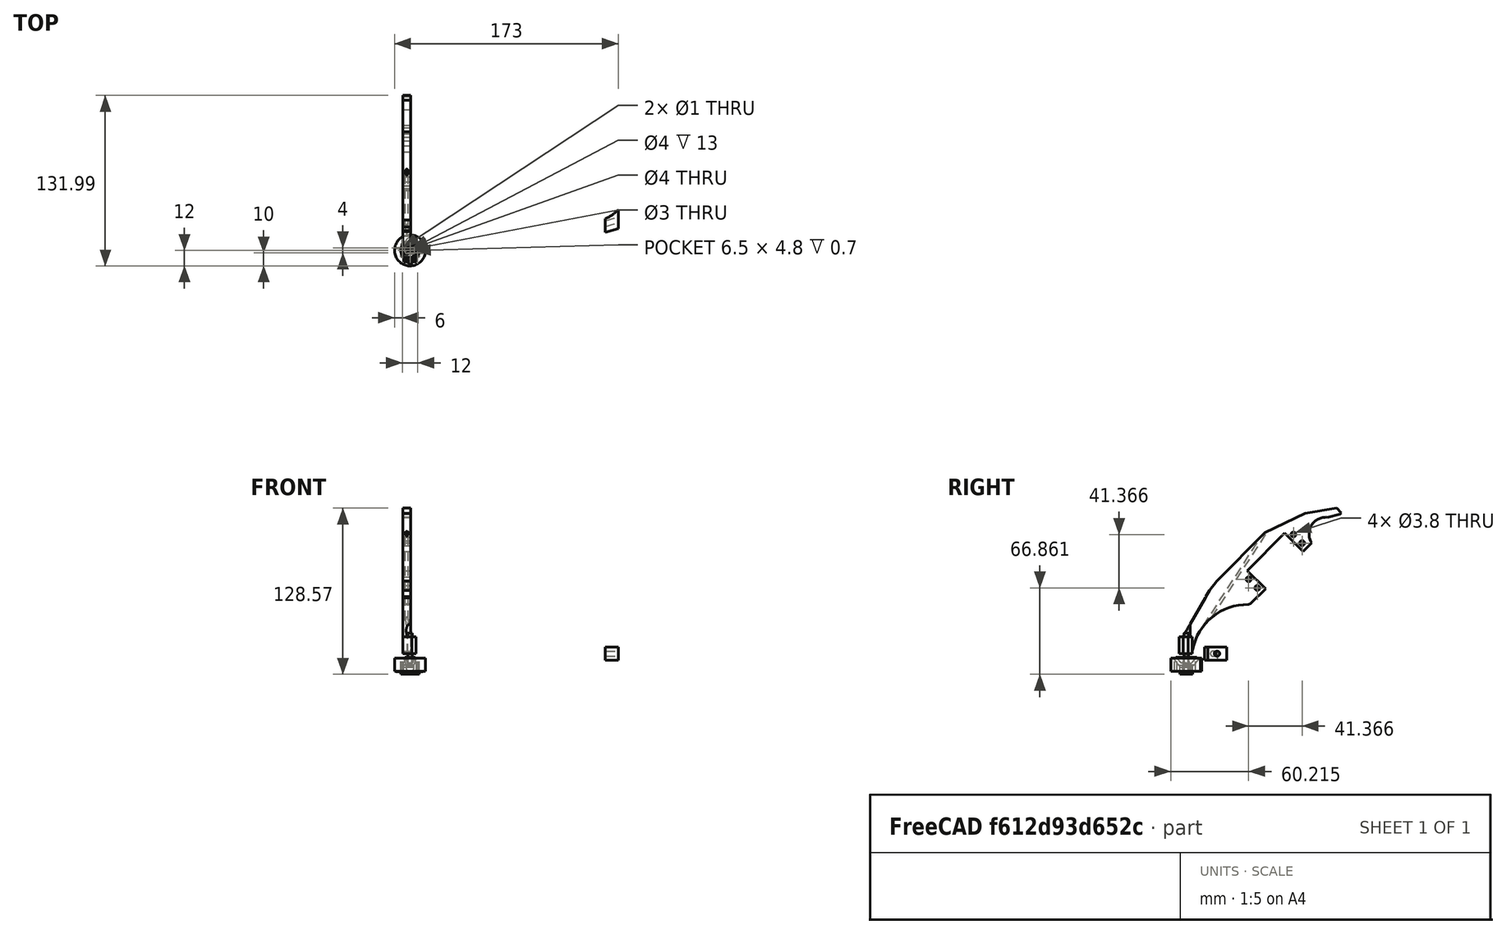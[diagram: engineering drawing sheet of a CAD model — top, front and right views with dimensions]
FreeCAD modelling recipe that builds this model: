
FCSTD DOCUMENT  (FreeCAD 0.16R6710 (Git))
Label: Feet sensor and leg 0.2
License: All rights reserved
LicenseURL: http://en.wikipedia.org/wiki/All_rights_reserved
objects: Part::Cut×37, Part::Cylinder×27, Part::Box×25, Part::Fuse×7, Part::Chamfer×4, Part::Sphere×3, Part::MultiCommon×2, Part::Cone×2, Part::FeaturePython×2, Part::Fillet×2, App::DocumentObjectGroup×1
note: 111 computed .brp shape members not serialized (recipe doc carries the construction recipe); baked Part::Feature solids carry a one-line shape summary decoded from their .brp

FEATURE [Part::Sphere] Sphere
  Angle1 = -90
  Angle2 = 90
  Angle3 = 360
  Radius = 3
FEATURE [Part::Cylinder] Cylinder
  Angle = 360
  Height = 10
  Radius = 1.5
FEATURE [Part::Box] Box  label="Cube"
  Height = 1
  Length = 6.5
  Placement = pos=(-3.25,-2.4,-4.2) rot=(0,0,1;0rad)
  Width = 4.8
FEATURE [Part::Cylinder] Cylinder001
  Angle = 360
  Height = 10
  Placement = pos=(-11,2,-3.7) rot=(0,1,0;1.5708rad)
  Radius = 0.25
FEATURE [Part::Cylinder] Cylinder002
  Angle = 360
  Height = 10
  Placement = pos=(0,-2,-3.7) rot=(0,1,0;1.5708rad)
  Radius = 0.25
FEATURE [Part::Box] Box001  label="Cube001"
  Height = 7.25
  Length = 14
  Placement = pos=(-7,-5,-6) rot=(0,0,1;0rad)
  Width = 10
FEATURE [Part::Box] Box002  label="Cube002"
  Height = 1
  Length = 6.5
  Placement = pos=(-3.25,-2.4,-4.2) rot=(0,0,1;0rad)
  Width = 4.8
FEATURE [Part::Cylinder] Cylinder003
  Angle = 360
  Height = 10
  Placement = pos=(-11,2,-3.7) rot=(0,1,0;1.5708rad)
  Radius = 0.25
FEATURE [Part::Cylinder] Cylinder004
  Angle = 360
  Height = 10
  Placement = pos=(0,-2,-3.7) rot=(0,1,0;1.5708rad)
  Radius = 0.25
FEATURE [Part::Fuse] Fusion
  Base = -> Cylinder003
  Tool = -> Cylinder004
FEATURE [Part::Fuse] Fusion001
  Base = -> Box002
  Tool = -> Fusion
FEATURE [Part::Box] Box003  label="Cube003"
  Height = 3
  Length = 10
  Placement = pos=(-5,-6,-3.5) rot=(0,0,1;0rad)
  Width = 12
FEATURE [Part::Cut] Cut
  Base = -> Box001
  Tool = -> Box003
FEATURE [Part::Cut] Cut001
  Base = -> Cut
  Tool = -> Fusion001
FEATURE [Part::Fuse] Fusion002
  Base = -> Cylinder001
  Tool = -> Cylinder002
FEATURE [Part::Fuse] Fusion003  label="Switch"
  Base = -> Box
  Tool = -> Fusion002
FEATURE [Part::Box] Box004  label="Cube004"
  Height = 5
  Length = 10
  Placement = pos=(-5,4,-3.55) rot=(0,0,1;0rad)
  Width = 3
FEATURE [Part::Sphere] Sphere001
  Angle1 = -90
  Angle2 = 90
  Angle3 = 360
  Radius = 3.1
FEATURE [Part::Cylinder] Cylinder005
  Angle = 360
  Height = 10
  Placement = pos=(0,0,0.5) rot=(0,0,1;0rad)
  Radius = 2.5
FEATURE [Part::Fuse] Fusion004
  Base = -> Sphere001
  Tool = -> Cylinder005
FEATURE [Part::Cut] Cut002
  Base = -> Cut001
  Tool = -> Fusion004
FEATURE [Part::Fuse] Fusion005  label="Ball and Screw"
  Base = -> Sphere
  Placement = pos=(0,0,-1) rot=(0,0,1;0rad)
  Tool = -> Cylinder
FEATURE [Part::Cut] Cut003
  Base = -> Cut001
  Tool = -> Fusion004
FEATURE [Part::Box] Box005  label="Cube005"
  Height = 8
  Length = 21
  Placement = pos=(-9,-7,-3.5) rot=(0,0,1;0rad)
  Width = 17
FEATURE [Part::Box] Box006  label="Cube006"
  Height = 12
  Length = 21
  Placement = pos=(-9,-7,-3.5) rot=(0,0,1;0rad)
  Width = 17
FEATURE [Part::Cut] Cut004  label="Bottom Switch holder"
  Base = -> Cut003
  Tool = -> Box005
FEATURE [Part::MultiCommon] Common  label="Ball and screw holder"
  Shapes = -> [Cut002,Box006]
FEATURE [Part::Cylinder] Cylinder006
  Angle = 360
  Height = 10
  Placement = pos=(0,0,-3.5) rot=(0,0,1;0rad)
  Radius = 12
FEATURE [Part::Box] Box007  label="Cube007"
  Height = 10
  Length = 10
  Placement = pos=(-5,-9,-3.5) rot=(0,0,1;0rad)
  Width = 20
FEATURE [Part::Cylinder] Cylinder007
  Angle = 360
  Height = 10
  Placement = pos=(0,0,-3.5) rot=(0,0,1;0rad)
  Radius = 7.1
FEATURE [Part::Cylinder] Cylinder008
  Angle = 360
  Height = 10
  Placement = pos=(0,0,-6.5) rot=(0,0,1;0rad)
  Radius = 7.1
FEATURE [Part::MultiCommon] Common002  label="Switch plate"
  Shapes = -> [Cut004,Cylinder008]
FEATURE [Part::Cylinder] Cylinder009
  Angle = 360
  Height = 13
  Placement = pos=(-6,2,-4) rot=(0,0,1;0rad)
  Radius = 0.5
FEATURE [Part::Cylinder] Cylinder010
  Angle = 360
  Height = 13
  Placement = pos=(6,-2,-4) rot=(0,0,1;0rad)
  Radius = 0.5
FEATURE [Part::Box] Box008  label="Cube008"
  Height = 12
  Length = 41
  Placement = pos=(42,14,-1) rot=(0,0,1;0rad)
  Width = 20
FEATURE [Part::Cylinder] Cylinder011
  Angle = 360
  Height = 12
  Placement = pos=(38,19.5,-1) rot=(0,0,1;0rad)
  Radius = 1.9
FEATURE [Part::Cylinder] Cylinder012
  Angle = 360
  Height = 12
  Placement = pos=(38,29,-1) rot=(0,0,1;0rad)
  Radius = 1.9
FEATURE [Part::Cylinder] Cylinder013
  Angle = 360
  Height = 12
  Placement = pos=(87,29,-1) rot=(0,0,1;0rad)
  Radius = 1.9
FEATURE [Part::Cylinder] Cylinder014
  Angle = 360
  Height = 12
  Placement = pos=(87,19.5,-1) rot=(0,0,1;0rad)
  Radius = 1.9
FEATURE [Part::Box] Box009  label="Cube009"
  Height = 6
  Length = 184
  Width = 34
FEATURE [Part::Box] Box010  label="Cube010"
  Height = 12
  Length = 37
  Width = 8
FEATURE [Part::Cylinder] Cylinder015
  Angle = 360
  Height = 10
  Placement = pos=(20,37,0) rot=(0,0,1;0rad)
  Radius = 13
FEATURE [Part::Cut] Cut008
  Base = -> Box009
  Tool = -> Box010
FEATURE [Part::Cut] Cut009
  Base = -> Cut008
  Tool = -> Cylinder015
FEATURE [Part::Cylinder] Cylinder016
  Angle = 360
  Height = 10
  Placement = pos=(132,63,0) rot=(0,0,1;0rad)
  Radius = 43
FEATURE [Part::Cut] Cut010
  Base = -> Cut009
  Tool = -> Cylinder016
FEATURE [Part::Box] Box011  label="Cube011"
  Height = 10
  Length = 41
  Placement = pos=(120,0,0) rot=(0,0,1;0rad)
  Width = 6
FEATURE [Part::Cut] Cut011
  Base = -> Cut010
  Tool = -> Box011
FEATURE [Part::Box] Box012  label="Cube012"
  Height = 10
  Length = 23
  Placement = pos=(161,0,0) rot=(0,0,1;0rad)
  Width = 17
FEATURE [Part::Cut] Cut012
  Base = -> Cut011
  Tool = -> Box012
FEATURE [Part::Box] Box013  label="Cube013"
  Height = 10
  Length = 13
  Placement = pos=(0,8,0) rot=(0,0,1;0rad)
  Width = 11
FEATURE [Part::Cut] Cut013
  Base = -> Cut012
  Tool = -> Box013
FEATURE [Part::Box] Box014  label="Cube014"
  Height = 10
  Length = 53
  Placement = pos=(-16,28,0) rot=(0,0,-1;0.628319rad)
  Width = 10
FEATURE [Part::Cut] Cut014
  Base = -> Cut013
  Tool = -> Box014
FEATURE [Part::Box] Box015  label="Cube015"
  Height = 10
  Length = 49
  Placement = pos=(16,5,0) rot=(0,0,-1;0.331613rad)
  Width = 10
FEATURE [Part::Cut] Cut015
  Base = -> Cut014
  Tool = -> Box015
FEATURE [Part::Box] Box016  label="Cube016"
  Height = 10
  Length = 76
  Placement = pos=(46,-7,0) rot=(0,0,1;0rad)
  Width = 10
FEATURE [Part::Cut] Cut016
  Base = -> Cut015
  Tool = -> Box016
FEATURE [Part::Box] Box017  label="Cube017"
  Height = 10
  Length = 65
  Placement = pos=(115,-7,0) rot=(0,0,1;0.261799rad)
  Width = 11
FEATURE [Part::Cut] Cut017
  Base = -> Cut016
  Tool = -> Box017
FEATURE [Part::Box] Box018  label="Cube018"
  Height = 10
  Length = 14
  Placement = pos=(174,10,0) rot=(0,0,1;0.279253rad)
  Width = 10
FEATURE [Part::Cut] Cut018
  Base = -> Cut017
  Tool = -> Box018
FEATURE [Part::Box] Box019  label="Cube019"
  Height = 10
  Length = 10
  Placement = pos=(106,-7,0) rot=(0,0,1;0.139626rad)
  Width = 10
FEATURE [Part::Cut] Cut019
  Base = -> Cut018
  Tool = -> Box019
FEATURE [Part::Cut] Cut020
  Base = -> Cut019
  Tool = -> Box008
FEATURE [Part::Cut] Cut021
  Base = -> Cut020
  Tool = -> Cylinder014
FEATURE [Part::Cut] Cut022
  Base = -> Cut021
  Tool = -> Cylinder013
FEATURE [Part::Cut] Cut023
  Base = -> Cut022
  Tool = -> Cylinder012
FEATURE [Part::Cut] Cut024
  Base = -> Cut023
  Tool = -> Cylinder011
FEATURE [Part::Chamfer] Chamfer
  Base = -> Cut024
  Edges = 1 edges r=6: [Edge36]
FEATURE [Part::Chamfer] Chamfer001
  Base = -> Chamfer
  Edges = 1 edges r=1: [Edge59]
FEATURE [Part::Box] Box020  label="Cube020"
  Height = 10
  Length = 10
  Placement = pos=(151,12,5) rot=(0,0,1;0rad)
  Width = 21
FEATURE [Part::Box] Box021  label="Cube021"
  Height = 13
  Length = 26
  Placement = pos=(161,15,-3) rot=(0,0,1;0rad)
  Width = 23
FEATURE [Part::Cut] Cut025
  Base = -> Chamfer001
  Placement = pos=(-5.5,-24,171) rot=(0,1,0;1.5708rad)
  Tool = -> Box021
FEATURE [Part::Cylinder] Cylinder017
  Angle = 360
  Height = 19
  Placement = pos=(132,63,0) rot=(0,0,1;0rad)
  Radius = 43
FEATURE [Part::Cut] Cut026
  Base = -> Box020
  Tool = -> Cylinder017
FEATURE [Part::Box] Box022  label="Cube022"
  Height = 20
  Length = 65
  Placement = pos=(115,-7,0) rot=(0,0,1;0.261799rad)
  Width = 11
FEATURE [Part::Cut] Cut027
  Base = -> Cut026
  Tool = -> Box022
FEATURE [Part::Cylinder] Cylinder018
  Angle = 360
  Height = 18
  Placement = pos=(146.076,19.1828,10) rot=(-0.146221,0.978386,0.146221;1.59265rad)
  Radius = 2
FEATURE [Part::Cut] Cut028
  Base = -> Cut027
  Tool = -> Cylinder018
FEATURE [Part::Cone] Cone
  Angle = 360
  Height = 7
  Placement = pos=(0,0,1) rot=(0,0,1;0rad)
  Radius1 = 3
  Radius2 = 5.5
FEATURE [Part::FeaturePython] Clone  label="Clone of Cone"  # Draft clone (typed FeaturePython)
  Objects = -> [Cone]
  Placement = pos=(0,0,1) rot=(0,0,1;0rad)
  Scale = (1,2,1)
FEATURE [Part::Box] Box023  label="Cube023"
  Height = 3.5
  Length = 10
  Placement = pos=(-5,-5,-4) rot=(0,0,1;0rad)
  Width = 10
FEATURE [Part::Cut] Cut029
  Base = -> Cylinder006
  Tool = -> Box023
FEATURE [Part::Cut] Cut030
  Base = -> Cut029
  Tool = -> Cylinder010
FEATURE [Part::Cut] Cut031
  Base = -> Cut030
  Tool = -> Cylinder009
FEATURE [Part::Cut] Cut032
  Base = -> Cut031
  Tool = -> Clone
FEATURE [Part::Cylinder] Cylinder019
  Angle = 360
  Height = 10
  Placement = pos=(0,0,-1) rot=(0,0,1;0rad)
  Radius = 1.5
FEATURE [Part::Cut] Cut033
  Base = -> Cut032
  Tool = -> Cylinder019
FEATURE [App::DocumentObjectGroup] Group  label="Not used"
  Group = -> [Box004,Common,Box007,Cylinder007,Cut028]
FEATURE [Part::Cone] Cone001
  Angle = 360
  Height = 6
  Placement = pos=(0,0,1) rot=(0,0,1;0rad)
  Radius1 = 2
  Radius2 = 4
FEATURE [Part::FeaturePython] Clone001  label="Clone of Cone001"  # Draft clone (typed FeaturePython)
  Objects = -> [Cone001]
  Placement = pos=(0,0,3) rot=(0,0,1;0rad)
  Scale = (1,2,0.75)
FEATURE [Part::Cylinder] Cylinder020
  Angle = 360
  Height = 16
  Placement = pos=(0,0,9) rot=(0,0,1;0rad)
  Radius = 2
FEATURE [Part::Sphere] Sphere002
  Angle1 = -90
  Angle2 = 90
  Angle3 = 360
  Placement = pos=(0,0,-3) rot=(0,0,1;0rad)
  Radius = 3.5
FEATURE [Part::Cut] Cut034  label="Foot"
  Base = -> Cut033
  Tool = -> Sphere002
FEATURE [Part::Cylinder] Cylinder021
  Angle = 360
  Height = 26
  Radius = 1.7
FEATURE [Part::Fillet] Fillet
  Base = -> Cut025
  Edges = 1 edges r=3: [Edge30]
FEATURE [Part::Cylinder] Cylinder022  label="Not used cylinder001"
  Angle = 360
  Height = 16
  Placement = pos=(0,-50,23) rot=(0,0,1;0rad)
  Radius = 3
FEATURE [Part::Fillet] Fillet001
  Base = -> Fillet
  Edges = 1 edges r=3: [Edge39]
FEATURE [Part::Box] Box024  label="Cube024"
  Height = 13
  Length = 10
  Placement = pos=(-5.5,-5.5,10) rot=(0,0,1;0rad)
  Width = 10
FEATURE [Part::Cut] Cut035
  Base = -> Fillet001
  Placement = pos=(0,-8,5) rot=(-1,0,0;0.785398rad)
  Tool = -> Cylinder022
FEATURE [Part::Cylinder] Cylinder023
  Angle = 360
  Height = 26
  Radius = 1.7
FEATURE [Part::Fuse] Fusion006
  Base = -> Box024
  Tool = -> Cut035
FEATURE [Part::Cylinder] Cylinder024
  Angle = 360
  Height = 16
  Placement = pos=(0,0,23) rot=(0,0,1;0rad)
  Radius = 3
FEATURE [Part::Cut] Cut036
  Base = -> Fusion006
  Tool = -> Cylinder024
FEATURE [Part::Cut] Cut037
  Base = -> Cut036
  Tool = -> Cylinder020
FEATURE [Part::Chamfer] Chamfer002
  Base = -> Cut037
  Edges = 1 edges r=3: [Edge13]
FEATURE [Part::Chamfer] Chamfer003
  Base = -> Chamfer002
  Edges = 1 edges r=3: [Edge21]
FEATURE [Part::Cylinder] Cylinder025
  Angle = 360
  Height = 96
  Placement = pos=(-2.5,14,31) rot=(-1,0,0;0.575959rad)
  Radius = 1
FEATURE [Part::Cut] Cut038  label="Leg"
  Base = -> Chamfer003
  Tool = -> Cylinder025
FEATURE [Part::Cylinder] Cylinder026
  Angle = 360
  Height = 16
  Placement = pos=(0,0,0.5) rot=(0,0,1;0rad)
  Radius = 2
FEATURE [Part::Cut] Cut039  label="Bottom of leg"
  Base = -> Clone001
  Tool = -> Cylinder026
